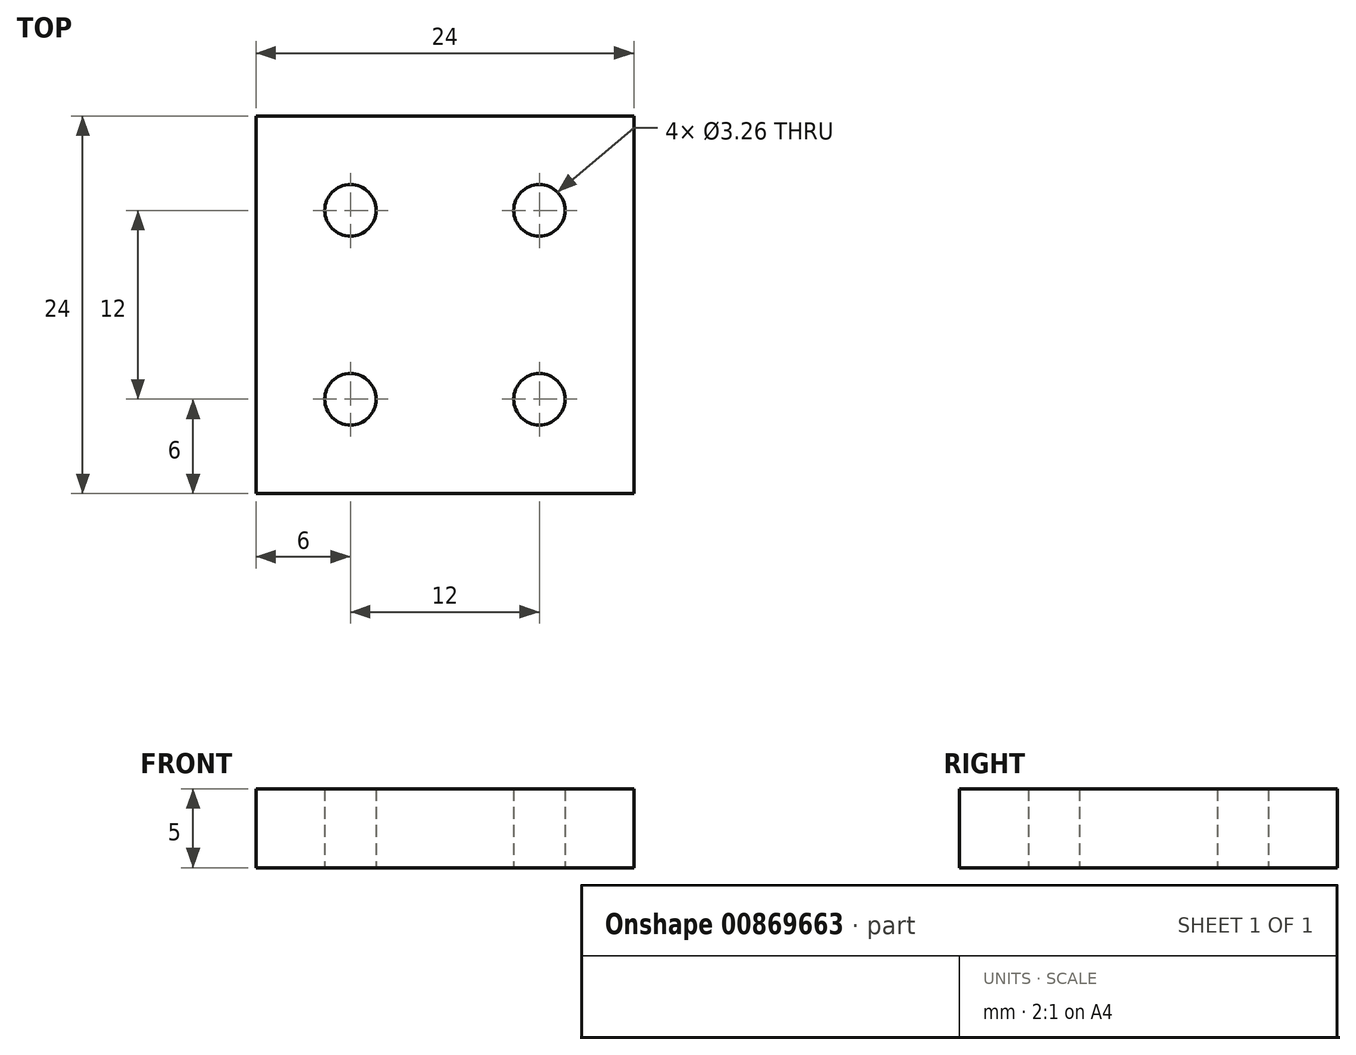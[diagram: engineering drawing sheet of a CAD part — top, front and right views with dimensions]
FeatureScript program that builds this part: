
annotation { "Feature Type Name" : "Feature", "Feature Type Description" : "" }
export const myFeature = defineFeature(function(context is Context, id is Id, definition is map)
    precondition{}
    {
        {
            var Q0;
            Q0=qCreatedBy(makeId("Top.planeOp"),FACE);
            var sketch = newSketch(context, id + "F0", { "sketchPlane" : qUnion([Q0])});
            skLineSegment(sketch, "E0.bottom", {"start": v(-12, 12) * mm, "end": v(12, 12) * mm});
            skLineSegment(sketch, "E0.top", {"start": v(-12, -12) * mm, "end": v(12, -12) * mm});
            skLineSegment(sketch, "E0.left", {"start": v(-12, 12) * mm, "end": v(-12, -12) * mm});
            skLineSegment(sketch, "E0.right", {"start": v(12, 12) * mm, "end": v(12, -12) * mm});
            skPoint(sketch, "E0.middle", {"position": v(0, 0) * mm});
            skLineSegment(sketch, "E1.bottom", {"start": v(-9.5, 9.5) * mm, "end": v(-2.5, 9.5) * mm});
            skLineSegment(sketch, "E1.top", {"start": v(-9.5, 2.5) * mm, "end": v(-2.5, 2.5) * mm});
            skLineSegment(sketch, "E1.left", {"start": v(-9.5, 9.5) * mm, "end": v(-9.5, 2.5) * mm});
            skLineSegment(sketch, "E1.right", {"start": v(-2.5, 9.5) * mm, "end": v(-2.5, 2.5) * mm});
            skLineSegment(sketch, "E2.MirrorCS", {"start": v(-9.5, -2.5) * mm, "end": v(-2.5, -2.5) * mm});
            skLineSegment(sketch, "E3.MirrorCS", {"start": v(-9.5, -9.5) * mm, "end": v(-9.5, -2.5) * mm});
            skLineSegment(sketch, "E4.MirrorCS", {"start": v(-9.5, -9.5) * mm, "end": v(-2.5, -9.5) * mm});
            skLineSegment(sketch, "E5.MirrorCS", {"start": v(-2.5, -9.5) * mm, "end": v(-2.5, -2.5) * mm});
            skLineSegment(sketch, "E6.MirrorCS", {"start": v(9.5, 9.5) * mm, "end": v(2.5, 9.5) * mm});
            skLineSegment(sketch, "E7.MirrorCS", {"start": v(2.5, 9.5) * mm, "end": v(2.5, 2.5) * mm});
            skLineSegment(sketch, "E8.MirrorCS", {"start": v(9.5, 9.5) * mm, "end": v(9.5, 2.5) * mm});
            skLineSegment(sketch, "E9.MirrorCS", {"start": v(9.5, 2.5) * mm, "end": v(2.5, 2.5) * mm});
            skLineSegment(sketch, "E10.MirrorCS", {"start": v(2.5, -9.5) * mm, "end": v(2.5, -2.5) * mm});
            skLineSegment(sketch, "E11.MirrorCS", {"start": v(9.5, -2.5) * mm, "end": v(2.5, -2.5) * mm});
            skLineSegment(sketch, "E12.MirrorCS", {"start": v(9.5, -9.5) * mm, "end": v(9.5, -2.5) * mm});
            skLineSegment(sketch, "E13.MirrorCS", {"start": v(9.5, -9.5) * mm, "end": v(2.5, -9.5) * mm});
            skCircle(sketch, "E14", {"center": v(-6, 6) * mm, "radius": 1.63 * mm});
            skCircle(sketch, "E15.MirrorC", {"center": v(6, 6) * mm, "radius": 1.63 * mm});
            skCircle(sketch, "E16.MirrorC", {"center": v(-6, -6) * mm, "radius": 1.63 * mm});
            skCircle(sketch, "E17.MirrorC", {"center": v(6, -6) * mm, "radius": 1.63 * mm});
            skSolve(sketch);
        }
        {
            var Q0;
            Q0=makeQuery(id+"F0.imprint","IMPRINT",FACE,{"disambiguationData":[TD([[makeQuery(id+"F0.imprint","IMPRINT",EDGE,{"derivedFrom":sQuery(id+"F0.wireOp",EDGE,"E0.bottom")}),-1.0]])]});
            var Q1;
            Q1=makeQuery(id+"F0.imprint","IMPRINT",FACE,{"disambiguationData":[TD([[makeQuery(id+"F0.imprint","IMPRINT",EDGE,{"derivedFrom":sQuery(id+"F0.wireOp",EDGE,"E1.bottom")}),-1.0]])]});
            var Q2;
            Q2=makeQuery(id+"F0.imprint","IMPRINT",FACE,{"disambiguationData":[TD([[makeQuery(id+"F0.imprint","IMPRINT",EDGE,{"derivedFrom":sQuery(id+"F0.wireOp",EDGE,"E6.MirrorCS")}),1.0]])]});
            var Q3;
            Q3=makeQuery(id+"F0.imprint","IMPRINT",FACE,{"disambiguationData":[TD([[makeQuery(id+"F0.imprint","IMPRINT",EDGE,{"derivedFrom":sQuery(id+"F0.wireOp",EDGE,"E10.MirrorCS")}),-1.0]])]});
            var Q4;
            Q4=makeQuery(id+"F0.imprint","IMPRINT",FACE,{"disambiguationData":[TD([[makeQuery(id+"F0.imprint","IMPRINT",EDGE,{"derivedFrom":sQuery(id+"F0.wireOp",EDGE,"E2.MirrorCS")}),-1.0]])]});
            extrude(context, id + "F1", {"entities" : qUnion([Q0, Q1, Q2, Q3, Q4]), "depth" : 5 * mm, "offsetDistance" : 25 * mm});
        }
    });
